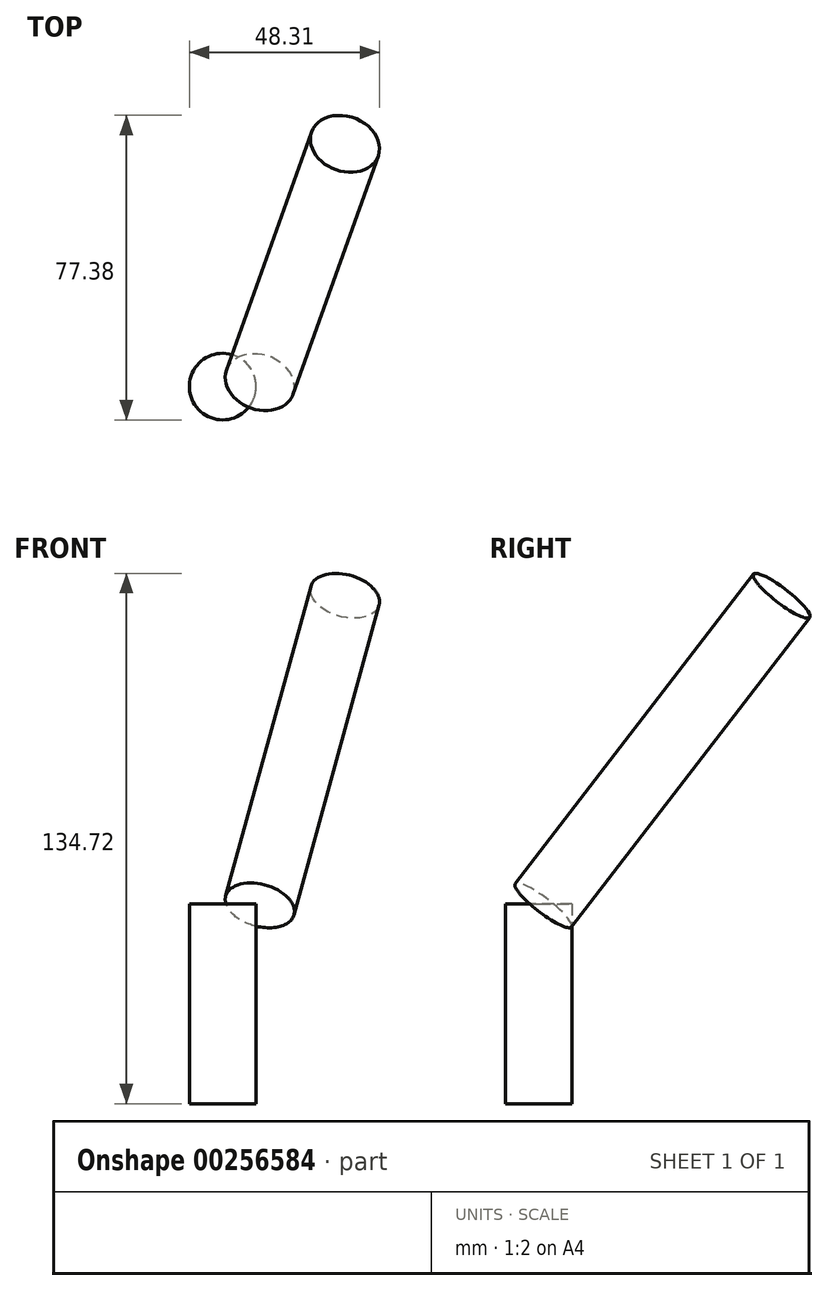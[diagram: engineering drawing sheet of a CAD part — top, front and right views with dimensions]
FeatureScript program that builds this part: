
annotation { "Feature Type Name" : "Feature", "Feature Type Description" : "" }
export const myFeature = defineFeature(function(context is Context, id is Id, definition is map)
    precondition{}
    {
        {
            var Q0;
            Q0=qCreatedBy(makeId("Top.planeOp"),FACE);
            var sketch = newSketch(context, id + "F0", { "sketchPlane" : qUnion([Q0])});
            skCircle(sketch, "E0", {"center": v(0, 0) * mm, "radius": 8.47 * mm});
            skSolve(sketch);
        }
        {
            var Q0;
            Q0 = qSketchRegion(id + "F0", true);
            extrude(context, id + "F1", {"entities" : qUnion([Q0]), "depth" : 50.8 * mm});
        }
        {
            var Q0;
            Q0=qCreatedBy(makeId("Top.planeOp"),FACE);
            var sketch = newSketch(context, id + "F2", { "sketchPlane" : qUnion([Q0])});
            skCircle(sketch, "E1", {"center": v(50.94, 0) * mm, "radius": 9 * mm});
            skSolve(sketch);
        }
        {
            var Q0;
            Q0 = qSketchRegion(id + "F2", true);
            extrude(context, id + "F3", {"entities" : qUnion([Q0]), "depth" : 101.6 * mm});
        }
        {
            var Q0;
            Q0=makeQuery(id+"F3.opExtrude","SWEPT_BODY",BODY,{"disambiguationData":[OSD([sQuery(id+"F2.wireOp",EDGE,"E1")])]});
            transform(context, id + "F4", {"entities" : qUnion([Q0]), "transformType" : TransformType.TRANSLATION_3D, "dx" : -41.9 * mm, "dy" : 0 * mm, "dz" : 50.8 * mm, "makeCopy" : false});
        }
        {
            var Q0;
            Q0=qCreatedBy(makeId("Front.planeOp"),FACE);
            var sketch = newSketch(context, id + "F5", { "sketchPlane" : qUnion([Q0])});
            skLineSegment(sketch, "E2", {"start": v(6.7, 46.73) * mm, "end": v(58.93, 95.95) * mm});
            skSolve(sketch);
        }
        {
            var Q0;
            Q0=makeQuery(id+"F3.opExtrude","SWEPT_BODY",BODY,{"disambiguationData":[OSD([sQuery(id+"F2.wireOp",EDGE,"E1")])]});
            var Q1;
            Q1=sQuery(id+"F5.wireOp",EDGE,"E2");
            transform(context, id + "F6", {"entities" : qUnion([Q0]), "transformType" : TransformType.ROTATION, "transformAxis" : qUnion([Q1]), "angle" : 55 * degree, "oppositeDirection" : true, "makeCopy" : false});
        }
    });
